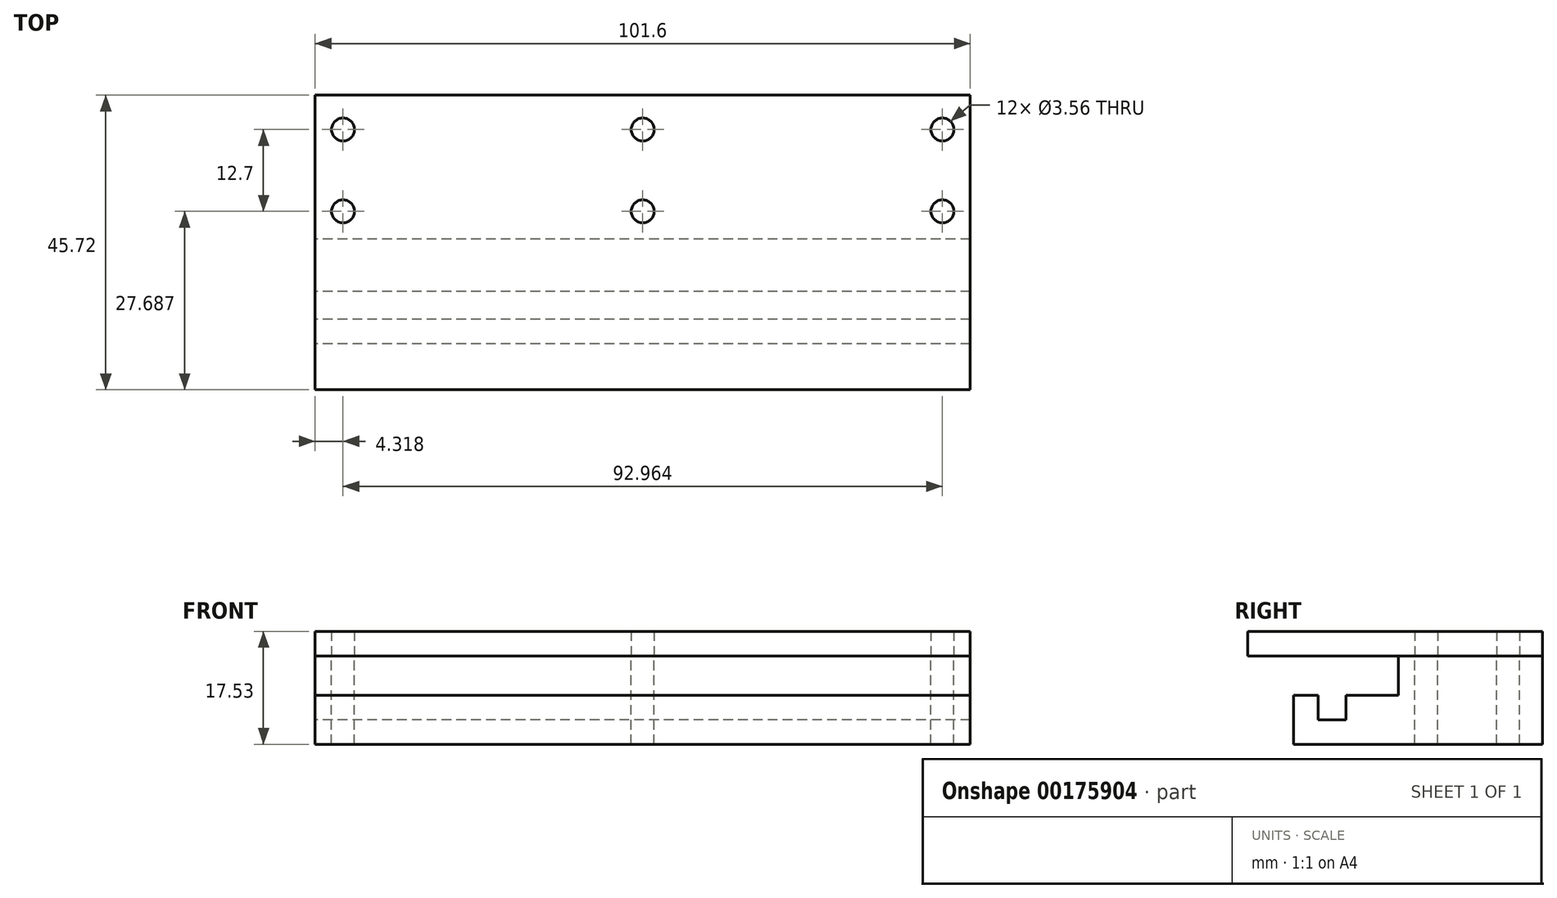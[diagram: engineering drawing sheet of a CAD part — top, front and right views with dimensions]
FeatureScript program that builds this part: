
annotation { "Feature Type Name" : "Feature", "Feature Type Description" : "" }
export const myFeature = defineFeature(function(context is Context, id is Id, definition is map)
    precondition{}
    {
        {
            var Q0;
            Q0=qCreatedBy(makeId("Right.planeOp"),FACE);
            var sketch = newSketch(context, id + "F0", { "sketchPlane" : qUnion([Q0])});
            skLineSegment(sketch, "E0.top", {"start": v(-6.45, -7.62) * mm, "end": v(32.16, -7.62) * mm});
            skLineSegment(sketch, "E0.left", {"start": v(-6.45, 0) * mm, "end": v(-6.45, -7.62) * mm});
            skLineSegment(sketch, "E0.right", {"start": v(32.16, 0) * mm, "end": v(32.16, -7.62) * mm});
            skLineSegment(sketch, "E1", {"start": v(-2.64, 0) * mm, "end": v(-2.64, -3.81) * mm});
            skLineSegment(sketch, "E2", {"start": v(-2.64, -3.81) * mm, "end": v(1.68, -3.81) * mm});
            skLineSegment(sketch, "E3", {"start": v(1.68, -3.81) * mm, "end": v(1.68, 0) * mm});
            skLineSegment(sketch, "E4", {"start": v(-6.45, 0) * mm, "end": v(-2.64, 0) * mm});
            skLineSegment(sketch, "E5", {"start": v(1.68, 0) * mm, "end": v(9.8, 0) * mm});
            skLineSegment(sketch, "E6", {"start": v(32.16, 0) * mm, "end": v(32.16, 6.1) * mm});
            skLineSegment(sketch, "E7", {"start": v(32.16, 6.1) * mm, "end": v(9.8, 6.1) * mm});
            skLineSegment(sketch, "E8", {"start": v(9.8, 6.1) * mm, "end": v(9.8, 0) * mm});
            skSolve(sketch);
        }
        {
            var Q0;
            Q0=makeQuery(id+"F0.imprint","IMPRINT",FACE,{"disambiguationData":[TD([[makeQuery(id+"F0.imprint","IMPRINT",EDGE,{"derivedFrom":sQuery(id+"F0.wireOp",EDGE,"E0.top")}),1.0]])]});
            extrude(context, id + "F1", {"entities" : qUnion([Q0]), "depth" : 101.6 * mm});
        }
        {
            var Q0;
            Q0=makeQuery(id+"F1.opExtrude","SWEPT_FACE",FACE,{"disambiguationData":[OSD([sQuery(id+"F0.wireOp",EDGE,"E7")])]});
            var sketch = newSketch(context, id + "F2", { "sketchPlane" : qUnion([Q0])});
            skCircle(sketch, "E9", {"center": v(97.28, 14.13) * mm, "radius": 1.78 * mm});
            skCircle(sketch, "E10", {"center": v(97.28, 26.83) * mm, "radius": 1.78 * mm});
            skCircle(sketch, "E11", {"center": v(4.32, 14.13) * mm, "radius": 1.78 * mm});
            skCircle(sketch, "E12", {"center": v(4.32, 26.83) * mm, "radius": 1.78 * mm});
            skCircle(sketch, "E13", {"center": v(50.8, 14.13) * mm, "radius": 1.78 * mm});
            skPoint(sketch, "E13.centerSnap0", {"position": v(50.8, 9.8) * mm});
            skCircle(sketch, "E14", {"center": v(50.8, 26.83) * mm, "radius": 1.78 * mm});
            skSolve(sketch);
        }
        {
            var Q0;
            Q0 = qSketchRegion(id + "F2", true);
            extrude(context, id + "F3", {"entities" : qUnion([Q0]), "operationType" : NewBodyOperationType.REMOVE, "endBound" : BoundingType.THROUGH_ALL, "oppositeDirection" : true, "depth" : 25.4 * mm});
        }
        {
            var Q0;
            Q0=qCreatedBy(makeId("Right.planeOp"),FACE);
            var sketch = newSketch(context, id + "F4", { "sketchPlane" : qUnion([Q0])});
            skLineSegment(sketch, "E15", {"start": v(-13.56, 6.1) * mm, "end": v(-13.56, 9.9) * mm});
            skLineSegment(sketch, "E16.0", {"start": v(32.16, 6.1) * mm, "end": v(9.8, 6.1) * mm});
            skLineSegment(sketch, "E17", {"start": v(-13.56, 6.1) * mm, "end": v(32.16, 6.1) * mm});
            skLineSegment(sketch, "E18", {"start": v(32.16, 9.9) * mm, "end": v(32.16, 6.1) * mm});
            skLineSegment(sketch, "E19", {"start": v(32.16, 9.9) * mm, "end": v(-13.56, 9.9) * mm});
            skSolve(sketch);
        }
        {
            var Q0;
            {var subQ0=sQuery(id+"F4.wireOp",EDGE,"E15");Q0=makeQuery(id+"F4.imprint","IMPRINT",FACE,{"disambiguationData":[TD([[makeQuery(id+"F4.imprint","IMPRINT",EDGE,{"derivedFrom":subQ0}),-1.0]])]});}
            var Q1;
            Q1=makeQuery(id+"F1.opExtrude","CAP_FACE",FACE,{"disambiguationData":[OSD([sQuery(id+"F0.wireOp",EDGE,"E0.top"),sQuery(id+"F0.wireOp",EDGE,"E0.left"),sQuery(id+"F0.wireOp",EDGE,"E0.right"),sQuery(id+"F0.wireOp",EDGE,"E1"),sQuery(id+"F0.wireOp",EDGE,"E2"),sQuery(id+"F0.wireOp",EDGE,"E3"),sQuery(id+"F0.wireOp",EDGE,"E4"),sQuery(id+"F0.wireOp",EDGE,"E5"),sQuery(id+"F0.wireOp",EDGE,"E6"),sQuery(id+"F0.wireOp",EDGE,"E7"),sQuery(id+"F0.wireOp",EDGE,"E8")])],"isStart":false});
            extrude(context, id + "F5", {"entities" : qUnion([Q0]), "endBound" : BoundingType.UP_TO_SURFACE, "endBoundEntityFace" : qUnion([Q1]), "depth" : 25.4 * mm});
        }
        {
            var Q0;
            Q0=makeQuery(id+"F5.opExtrude","SWEPT_FACE",FACE,{"disambiguationData":[OSD([sQuery(id+"F4.wireOp",EDGE,"E17")])]});
            var sketch = newSketch(context, id + "F6", { "sketchPlane" : qUnion([Q0])});
            skCircle(sketch, "E20.0", {"center": v(97.28, -14.13) * mm, "radius": 1.78 * mm});
            skCircle(sketch, "E20.1", {"center": v(50.8, -14.13) * mm, "radius": 1.78 * mm});
            skCircle(sketch, "E20.2", {"center": v(4.32, -14.13) * mm, "radius": 1.78 * mm});
            skCircle(sketch, "E20.3", {"center": v(4.32, -26.83) * mm, "radius": 1.78 * mm});
            skCircle(sketch, "E20.4", {"center": v(50.8, -26.83) * mm, "radius": 1.78 * mm});
            skCircle(sketch, "E20.5", {"center": v(97.28, -26.83) * mm, "radius": 1.78 * mm});
            skSolve(sketch);
        }
        {
            var Q0;
            Q0 = qSketchRegion(id + "F6", true);
            extrude(context, id + "F7", {"entities" : qUnion([Q0]), "operationType" : NewBodyOperationType.REMOVE, "endBound" : BoundingType.THROUGH_ALL, "oppositeDirection" : true, "depth" : 25.4 * mm});
        }
    });
